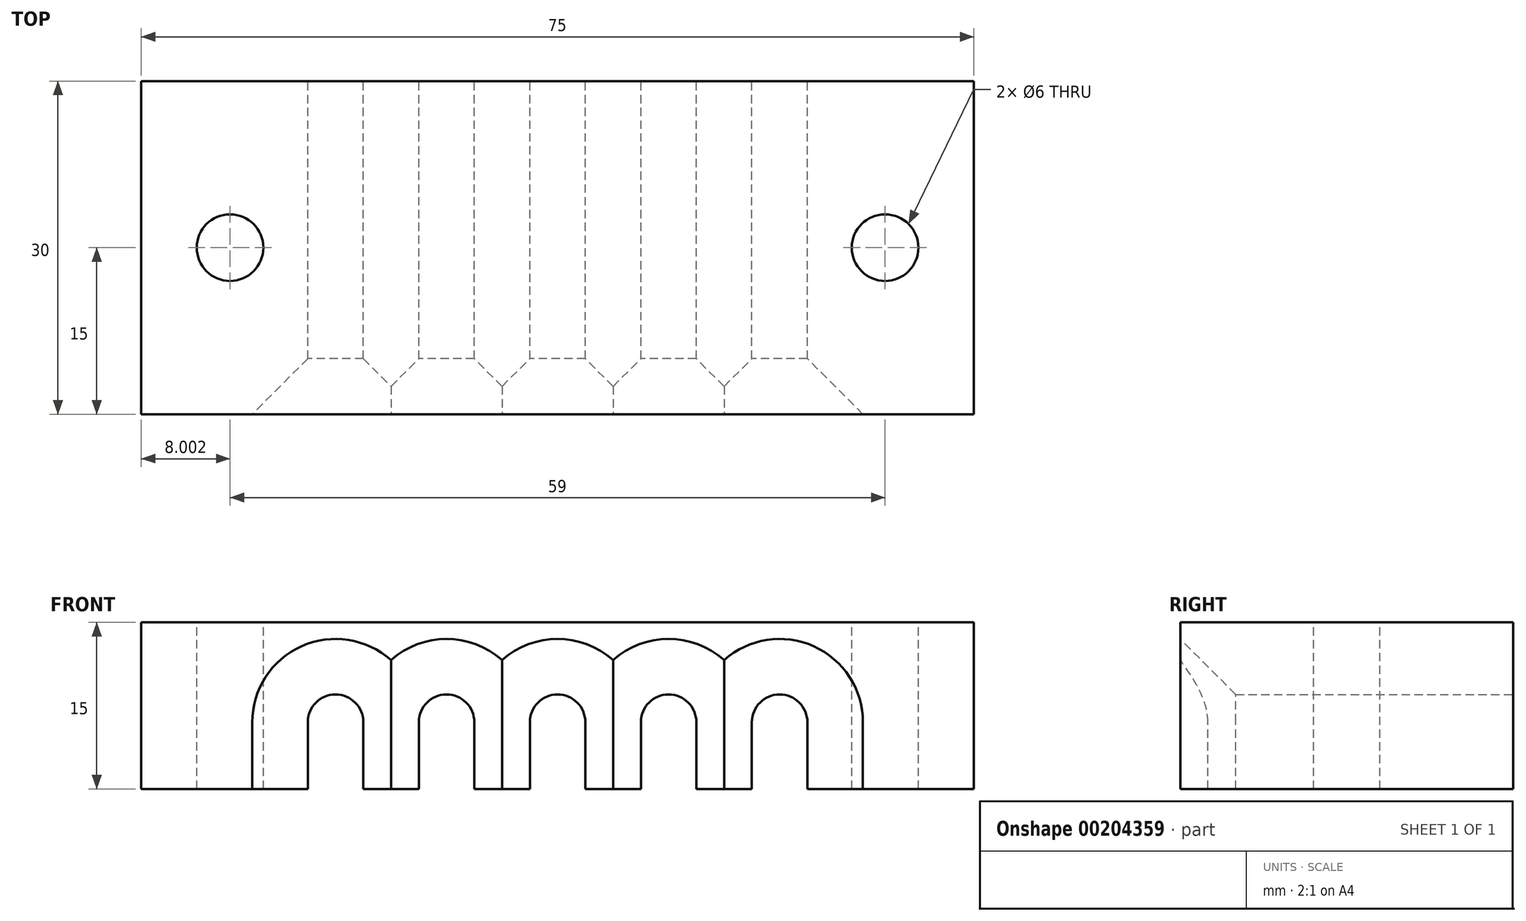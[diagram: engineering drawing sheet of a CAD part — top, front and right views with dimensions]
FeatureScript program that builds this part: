
annotation { "Feature Type Name" : "Feature", "Feature Type Description" : "" }
export const myFeature = defineFeature(function(context is Context, id is Id, definition is map)
    precondition{}
    {
        {
            var Q0;
            Q0=qCreatedBy(makeId("Front.planeOp"),FACE);
            var sketch = newSketch(context, id + "F0", { "sketchPlane" : qUnion([Q0])});
            skLineSegment(sketch, "E0.bottom", {"start": v(-45.38, 22.25) * mm, "end": v(29.62, 22.25) * mm});
            skLineSegment(sketch, "E0.top", {"start": v(-45.38, 7.25) * mm, "end": v(-30.38, 7.25) * mm});
            skLineSegment(sketch, "E0.left", {"start": v(-45.38, 22.25) * mm, "end": v(-45.38, 7.25) * mm});
            skLineSegment(sketch, "E0.right", {"start": v(29.62, 22.25) * mm, "end": v(29.62, 7.25) * mm});
            skLineSegment(sketch, "E1.left", {"start": v(-30.38, 7.25) * mm, "end": v(-30.38, 13.25) * mm});
            skLineSegment(sketch, "E1.right", {"start": v(-25.38, 7.25) * mm, "end": v(-25.38, 13.25) * mm});
            skArc(sketch, "E2", {"start": v(-25.38, 13.25) * mm, "mid": v(-27.88, 15.75) * mm, "end": v(-30.38, 13.25) * mm});
            skLineSegment(sketch, "E3.trimOffspring", {"start": v(-25.38, 7.25) * mm, "end": v(-20.38, 7.25) * mm});
            skLineSegment(sketch, "E4.left", {"start": v(-15.38, 13.25) * mm, "end": v(-15.38, 7.25) * mm});
            skLineSegment(sketch, "E4.right", {"start": v(-20.38, 13.25) * mm, "end": v(-20.38, 7.25) * mm});
            skLineSegment(sketch, "E5.left", {"start": v(-5.38, 13.25) * mm, "end": v(-5.38, 7.25) * mm});
            skLineSegment(sketch, "E6.left", {"start": v(4.62, 13.25) * mm, "end": v(4.62, 7.25) * mm});
            skLineSegment(sketch, "E6.right", {"start": v(-0.38, 13.25) * mm, "end": v(-0.38, 7.25) * mm});
            skLineSegment(sketch, "E7.left", {"start": v(14.62, 13.25) * mm, "end": v(14.62, 7.25) * mm});
            skLineSegment(sketch, "E7.right", {"start": v(9.62, 13.25) * mm, "end": v(9.62, 7.25) * mm});
            skArc(sketch, "E8", {"start": v(-15.38, 13.25) * mm, "mid": v(-17.88, 15.75) * mm, "end": v(-20.38, 13.25) * mm});
            skArc(sketch, "E9", {"start": v(-5.38, 13.25) * mm, "mid": v(-7.88, 15.75) * mm, "end": v(-10.38, 13.25) * mm});
            skArc(sketch, "E10", {"start": v(4.62, 13.25) * mm, "mid": v(2.12, 15.75) * mm, "end": v(-0.38, 13.25) * mm});
            skArc(sketch, "E11", {"start": v(14.62, 13.25) * mm, "mid": v(12.12, 15.75) * mm, "end": v(9.62, 13.25) * mm});
            skLineSegment(sketch, "E12.trimOffspring", {"start": v(-15.38, 7.25) * mm, "end": v(-10.38, 7.25) * mm});
            skLineSegment(sketch, "E13.trimOffspring", {"start": v(-5.38, 7.25) * mm, "end": v(-0.38, 7.25) * mm});
            skLineSegment(sketch, "E14.trimOffspring", {"start": v(4.62, 7.25) * mm, "end": v(9.62, 7.25) * mm});
            skLineSegment(sketch, "E15.trimOffspring", {"start": v(14.62, 7.25) * mm, "end": v(29.62, 7.25) * mm});
            skLineSegment(sketch, "E16", {"start": v(-10.38, 13.25) * mm, "end": v(-10.38, 7.25) * mm});
            skSolve(sketch);
        }
        {
            var Q0;
            Q0 = qSketchRegion(id + "F0", true);
            extrude(context, id + "F1", {"entities" : qUnion([Q0]), "depth" : 30 * mm});
        }
        {
            var Q0;
            Q0=makeQuery(id+"F1.opExtrude","SWEPT_FACE",FACE,{"disambiguationData":[OSD([sQuery(id+"F0.wireOp",EDGE,"E0.bottom")])]});
            var sketch = newSketch(context, id + "F2", { "sketchPlane" : qUnion([Q0])});
            skPoint(sketch, "E17", {"position": v(-37.38, -15) * mm});
            skPoint(sketch, "E18", {"position": v(21.62, -15) * mm});
            skSolve(sketch);
        }
        {
            var Q0;
            Q0=sQuery(id+"F2.wireOp",VERTEX,"E17");
            var Q1;
            Q1=sQuery(id+"F2.wireOp",VERTEX,"E18");
            var Q2;
            Q2=makeQuery(id+"F1.opExtrude","SWEPT_BODY",BODY,{"disambiguationData":[OSD([sQuery(id+"F0.wireOp",EDGE,"E0.bottom"),sQuery(id+"F0.wireOp",EDGE,"E0.top"),sQuery(id+"F0.wireOp",EDGE,"E0.left"),sQuery(id+"F0.wireOp",EDGE,"E0.right"),sQuery(id+"F0.wireOp",EDGE,"E1.left"),sQuery(id+"F0.wireOp",EDGE,"E1.right"),sQuery(id+"F0.wireOp",EDGE,"E2"),sQuery(id+"F0.wireOp",EDGE,"E3.trimOffspring"),sQuery(id+"F0.wireOp",EDGE,"E4.left"),sQuery(id+"F0.wireOp",EDGE,"E4.right"),sQuery(id+"F0.wireOp",EDGE,"E5.left"),sQuery(id+"F0.wireOp",EDGE,"E6.left"),sQuery(id+"F0.wireOp",EDGE,"E6.right"),sQuery(id+"F0.wireOp",EDGE,"E7.left"),sQuery(id+"F0.wireOp",EDGE,"E7.right"),sQuery(id+"F0.wireOp",EDGE,"E8"),sQuery(id+"F0.wireOp",EDGE,"E9"),sQuery(id+"F0.wireOp",EDGE,"E10"),sQuery(id+"F0.wireOp",EDGE,"E11"),sQuery(id+"F0.wireOp",EDGE,"E12.trimOffspring"),sQuery(id+"F0.wireOp",EDGE,"E13.trimOffspring"),sQuery(id+"F0.wireOp",EDGE,"E14.trimOffspring"),sQuery(id+"F0.wireOp",EDGE,"E15.trimOffspring"),sQuery(id+"F0.wireOp",EDGE,"E16")])]});
            hole(context, id + "F3", {"style" : HoleStyle.SIMPLE, "endStyle" : HoleEndStyle.THROUGH, "holeDiameter" : 6 * mm, "locations" : qUnion([Q0, Q1]), "scope" : qUnion([Q2]), "isTappedThrough" : true});
        }
        {
            var Q0;
            Q0=makeQuery(id+"F1.opExtrude","CAP_EDGE",EDGE,{"disambiguationData":[OSD([sQuery(id+"F0.wireOp",EDGE,"E1.left")])],"isStart":false});
            var Q1;
            Q1=makeQuery(id+"F1.opExtrude","CAP_EDGE",EDGE,{"disambiguationData":[OSD([sQuery(id+"F0.wireOp",EDGE,"E4.right")])],"isStart":false});
            var Q2;
            Q2=makeQuery(id+"F1.opExtrude","CAP_EDGE",EDGE,{"disambiguationData":[OSD([sQuery(id+"F0.wireOp",EDGE,"E16")])],"isStart":false});
            var Q3;
            Q3=makeQuery(id+"F1.opExtrude","CAP_EDGE",EDGE,{"disambiguationData":[OSD([sQuery(id+"F0.wireOp",EDGE,"E6.right")])],"isStart":false});
            var Q4;
            Q4=makeQuery(id+"F1.opExtrude","CAP_EDGE",EDGE,{"disambiguationData":[OSD([sQuery(id+"F0.wireOp",EDGE,"E7.right")])],"isStart":false});
            chamfer(context, id + "F4", {"entities" : qUnion([Q0, Q1, Q2, Q3, Q4]), "width" : 5 * mm, "tangentPropagation" : true});
        }
    });
